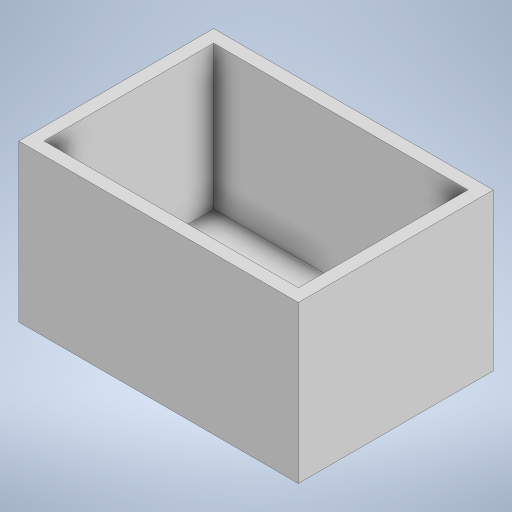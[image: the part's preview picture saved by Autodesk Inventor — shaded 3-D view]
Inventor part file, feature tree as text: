
AUTODESK INVENTOR PART (.ipt)
format: ipt  version: 2023 (Build 270158000, 158)  size: 247,808 bytes
history: native  units: mm
features: extrude x6, sketch x5, other x1
ambient origin geometry x8: Origin, YZ Plane, XZ Plane, XY Plane, X Axis, Y Axis, Z Axis, Center Point
bodies: Body1 (feature_tree)
feature tree (12):
  other  "솔리드1"
  sketch  "스케치1"
  extrude  "돌출1"  Depth=60.0mm
  extrude  "돌출2"  Depth=40.0mm
  extrude  "돌출3"  Depth=3.0mm
  extrude  "돌출4"  Depth=3.0mm TaperAngle=0.0deg
  extrude  "돌출5"  Depth=34.0mm TaperAngle=0.0deg
  extrude  "돌출6"  Depth=2.0mm
  sketch  "스케치2"
  sketch  "스케치3"
  sketch  "스케치4"
  sketch  "스케치5"
